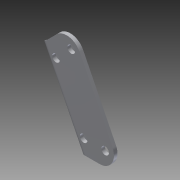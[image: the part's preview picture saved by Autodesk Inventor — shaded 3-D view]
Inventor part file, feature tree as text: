
AUTODESK INVENTOR PART (.ipt)
format: ipt  version: 2014 SP1 (Build 180222100, 222)  size: 229,888 bytes
history: native  units: in
note: dims shown in document units (in); Inventor stores cm internally (conversion verified against a paired STEP export)
features: other x4, sketch x1
ambient origin geometry x8: Origin, YZ Plane, XZ Plane, XY Plane, X Axis, Y Axis, Z Axis, Center Point
bodies: Solid1 (feature_tree)
feature tree (5):
  other  "V5 Shooter Frame Side Connector P1.ipt"
  other  "Solid1::V5 Shooter Frame Side Connector P1.ipt"
  sketch  "Sketch1"  dims[d0=0.3937in]
  other  "TaggingFeature1"
  other  "Definition1"
